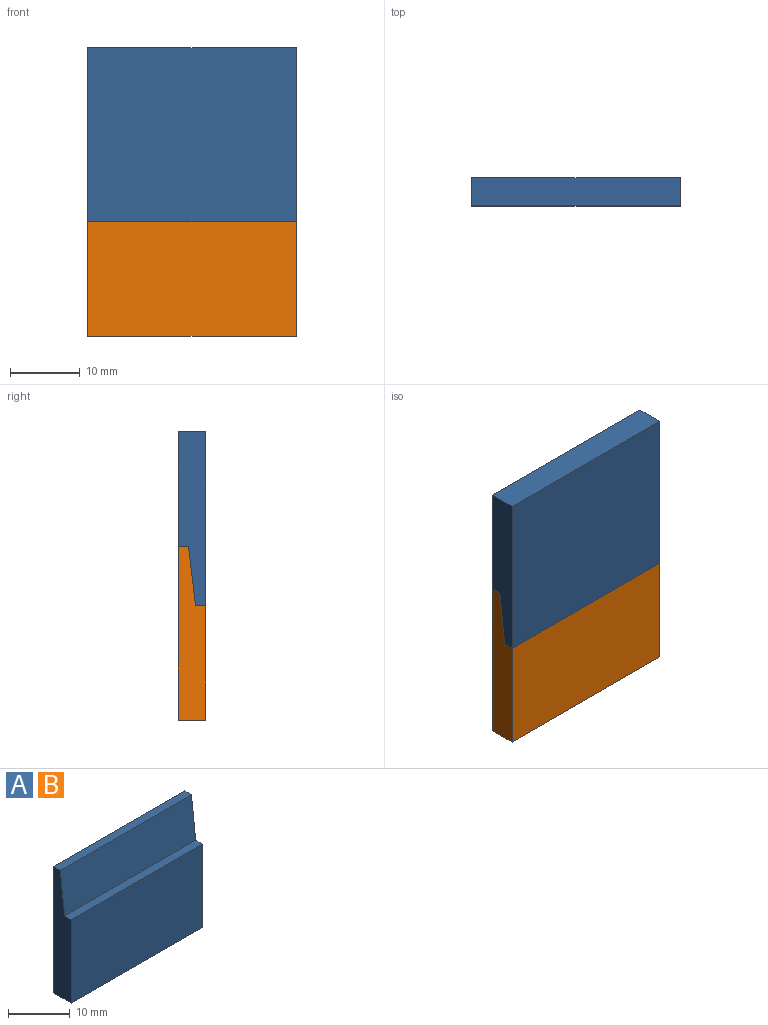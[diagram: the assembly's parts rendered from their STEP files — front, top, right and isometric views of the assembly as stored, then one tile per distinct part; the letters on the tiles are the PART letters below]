
ASSEMBLY  parts=2 mates=1
PART A: 8 faces, bbox 30x4x25 mm
  f0: plane 30x25mm, normal (0,1,0), area 750mm2, adj f1,f5,f6,f7
  f1: plane 30x1.5mm, normal (0,0,1), area 45mm2, adj f0,f2,f6,f7
  f2: plane 30x8.5mm, normal (0,-0.99,0.12), area 256.8mm2, adj f1,f3,f6,f7
  f3: plane 30x1.5mm, normal (0,0,1), area 45mm2, adj f2,f4,f6,f7
  f4: plane 30x16.5mm, normal (0,-1,0), area 495mm2, adj f3,f5,f6,f7
  f5: plane 30x4mm, normal (0,0,-1), area 120mm2, adj f0,f4,f6,f7
  f6: plane 25x4mm, normal (1,0,0), area 83mm2, adj f0,f1,f2,f3,f4,f5
  f7: plane 25x4mm, normal (-1,0,0), area 83mm2, adj f0,f1,f2,f3,f4,f5
PART B: same geometry as A
PLACE A rot(axis=(1,0,0),180deg) t=(42.44,-0.18,8.62)mm
PLACE B t=(42.44,-0.18,-7.88)mm
MATE fastened A.f2 <-> B.f2  axis (0,0.99,-0.12) through (27.44,-0.18,0.37)mm
